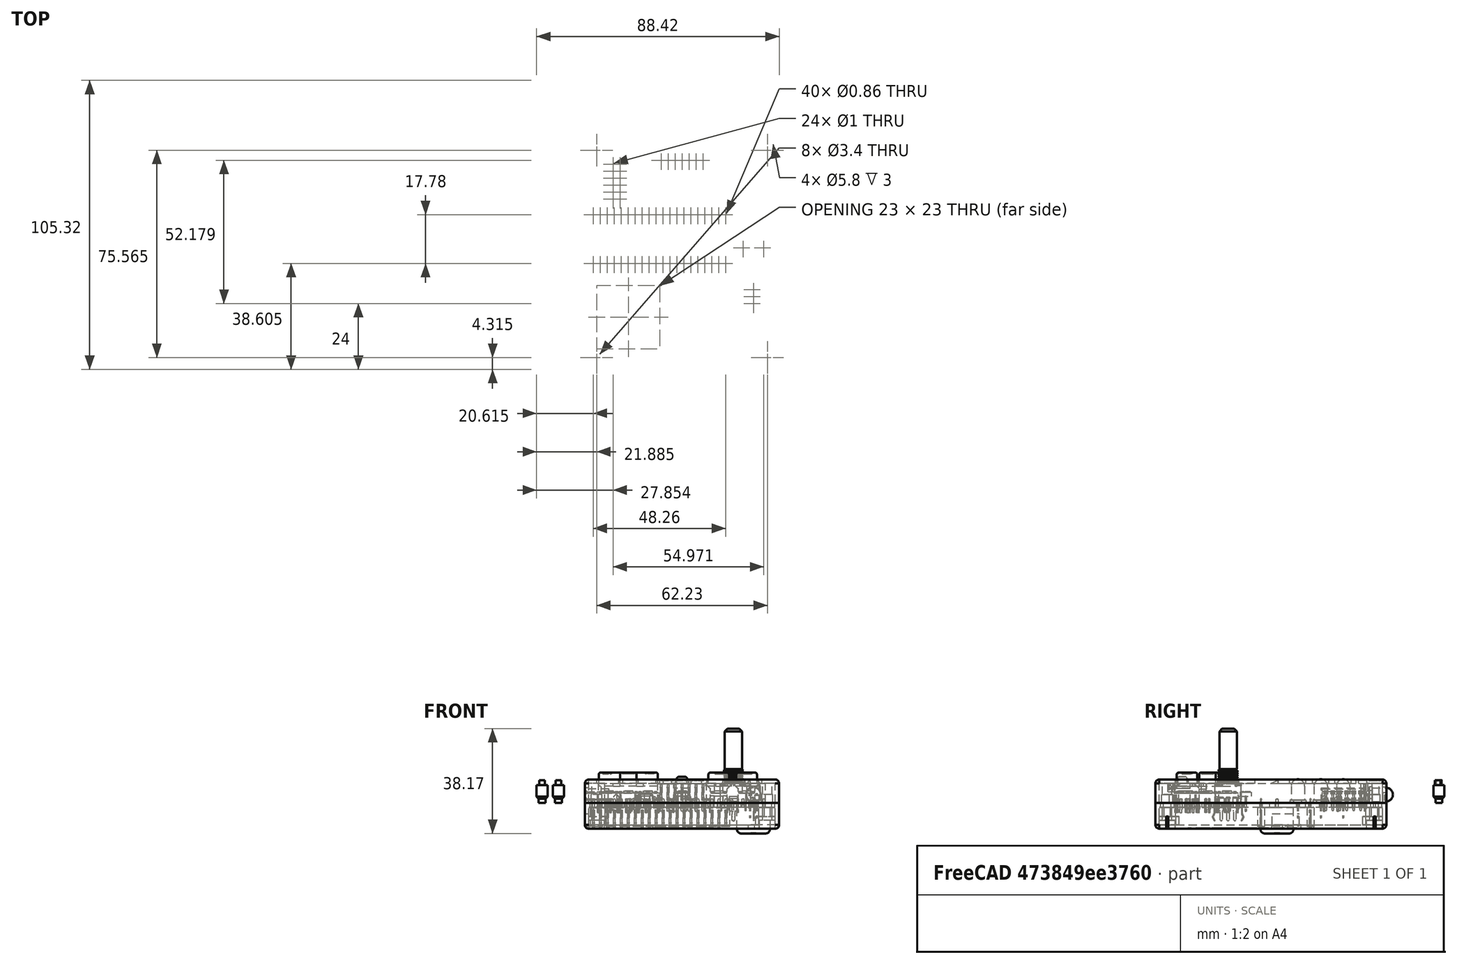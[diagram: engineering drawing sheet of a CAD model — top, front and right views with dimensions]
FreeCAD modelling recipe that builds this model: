
FCSTD DOCUMENT  (FreeCAD 0.19R24276 (Git))
Label: case
License: Creative Commons Attribution-ShareAlike
LicenseURL: http://creativecommons.org/licenses/by-sa/4.0/
objects: Part::FeaturePython×45, Part::Extrusion×42, Part::MultiFuse×27, Part::Cut×25, Part::Feature×22, Part::Part2DObjectPython×20, Part::Box×13, Part::Cylinder×11, Part::Fillet×6, Part::Chamfer×3, Part::Thickness×2
note: 216 computed .brp shape members not serialized (recipe doc carries the construction recipe); baked Part::Feature solids carry a one-line shape summary decoded from their .brp

FEATURE [Part::Cylinder] Cylinder
  Angle = 360
  AttacherType = Attacher::AttachEngine3D
  Height = 5
  Radius = 2
FEATURE [Part::Cylinder] Cylinder001
  Angle = 360
  AttacherType = Attacher::AttachEngine3D
  Height = 1.5
  Placement = pos=(0,0,5) rot=(0,0,1;0rad)
  Radius = 1.25
FEATURE [Part::Cylinder] Cylinder002
  Angle = 360
  AttacherType = Attacher::AttachEngine3D
  Height = 1.8
  Placement = pos=(0,0,-1.8) rot=(0,0,1;0rad)
  Radius = 1
FEATURE [Part::Chamfer] Chamfer
  Base = -> Cylinder
  Edges = 1 edges r=0.75: [Edge1]
FEATURE [Part::FeaturePython] Clone  label="Cylinder003"  # Draft clone (typed FeaturePython)
  AttacherType = Attacher::AttachEngine3D
  Fuse = false
  Objects = -> [Cylinder001]
  Placement = pos=(0,-6,5) rot=(0,0,1;0rad)
  Scale = (1,1,1)
FEATURE [Part::FeaturePython] Clone001  label="Cylinder004"  # Draft clone (typed FeaturePython)
  AttacherType = Attacher::AttachEngine3D
  Fuse = false
  Objects = -> [Cylinder002]
  Placement = pos=(0,-6.4,-1.8) rot=(0,0,1;0rad)
  Scale = (1,1,1)
FEATURE [Part::FeaturePython] Clone002  label="Chamfer001"  # Draft clone (typed FeaturePython)
  AttacherType = Attacher::AttachEngine3D
  Fuse = false
  Objects = -> [Chamfer]
  Placement = pos=(0,-6,0) rot=(0,0,1;0rad)
  Scale = (1,1,1)
FEATURE [Part::MultiFuse] Fusion  label="spacer_desviado"
  Placement = pos=(-45,65,6.5) rot=(0,1,0;3.14159rad)
  Refine = true
  Shapes = -> [Clone,Clone002,Clone001]
FEATURE [Part::MultiFuse] Fusion001  label="spacer_recto"
  Placement = pos=(-51,59,6.5) rot=(0,1,0;3.14159rad)
  Refine = true
  Shapes = -> [Cylinder001,Cylinder002,Chamfer]
FEATURE [Part::Feature] Wire
  shape: bbox 21.5 x 21.5 x 2e-07 mm, 0 faces, 0 solids (baked)
FEATURE [Part::Extrusion] Extrude
  Base = -> Wire
  Dir = (0,0,1)
  DirMode = 2
  FaceMakerClass = Part::FaceMakerBullseye
  LengthFwd = 5
  LengthRev = 0
  Solid = true
  Symmetric = false
FEATURE [Part::Box] Box  label="Cube"
  AttacherType = Attacher::AttachEngine3D
  Height = 1
  Length = 2.5
  Placement = pos=(3,-5.5,0) rot=(0,0,1;0rad)
  Width = 2.5
FEATURE [Part::FeaturePython] Clone003  label="Cube001"  # Draft clone (typed FeaturePython)
  AttacherType = Attacher::AttachEngine3D
  Fuse = false
  Objects = -> [Box]
  Placement = pos=(3,3,0) rot=(0,0,1;0rad)
  Scale = (1,1,1)
FEATURE [Part::FeaturePython] Clone004  label="Cube002"  # Draft clone (typed FeaturePython)
  AttacherType = Attacher::AttachEngine3D
  Fuse = false
  Objects = -> [Clone003]
  Placement = pos=(-5.5,3,0) rot=(0,0,1;0rad)
  Scale = (1,1,1)
FEATURE [Part::FeaturePython] Clone005  label="Cube003"  # Draft clone (typed FeaturePython)
  AttacherType = Attacher::AttachEngine3D
  Fuse = false
  Objects = -> [Clone004]
  Placement = pos=(-5.5,-5.5,0) rot=(0,0,1;0rad)
  Scale = (1,1,1)
FEATURE [Part::Feature] Wire001
  shape: bbox 4.4 x 2.2 x 2e-07 mm, 0 faces, 0 solids (baked)
FEATURE [Part::Feature] Wire002
  shape: bbox 4.4 x 0.5 x 2e-07 mm, 0 faces, 0 solids (baked)
FEATURE [Part::Extrusion] Extrude001
  Base = -> Wire001
  Dir = (0,0,-1)
  DirMode = 2
  FaceMakerClass = Part::FaceMakerBullseye
  LengthFwd = 0.5
  LengthRev = 0
  Placement = pos=(-1e-16,0,0.2) rot=(0,0,1;0rad)
  Solid = true
  Symmetric = false
FEATURE [Part::Extrusion] Extrude002
  Base = -> Wire002
  Dir = (0,0,1)
  DirMode = 2
  FaceMakerClass = Part::FaceMakerBullseye
  LengthFwd = -0.5
  LengthRev = 0
  Placement = pos=(-1e-16,0,0.2) rot=(0,0,1;0rad)
  Solid = true
  Symmetric = false
FEATURE [Part::FeaturePython] Clone006  label="Extrude003"  # Draft clone (typed FeaturePython)
  AttacherType = Attacher::AttachEngine3D
  Fuse = false
  Objects = -> [Extrude001]
  Placement = pos=(-1e-16,-4e-15,0.2) rot=(0,0,1;1.5708rad)
  Scale = (1,1,1)
FEATURE [Part::FeaturePython] Clone007  label="Extrude004"  # Draft clone (typed FeaturePython)
  AttacherType = Attacher::AttachEngine3D
  Fuse = false
  Objects = -> [Extrude002]
  Placement = pos=(-1e-16,-4e-15,0.2) rot=(0,0,1;1.5708rad)
  Scale = (1,1,1)
FEATURE [Part::FeaturePython] Clone008  label="Extrude005"  # Draft clone (typed FeaturePython)
  AttacherType = Attacher::AttachEngine3D
  Fuse = false
  Objects = -> [Extrude001]
  Placement = pos=(1e-15,0,0.2) rot=(0,0,1;3.14159rad)
  Scale = (1,1,1)
FEATURE [Part::FeaturePython] Clone009  label="Extrude006"  # Draft clone (typed FeaturePython)
  AttacherType = Attacher::AttachEngine3D
  Fuse = false
  Objects = -> [Extrude002]
  Placement = pos=(1e-15,0,0.2) rot=(0,0,1;3.14159rad)
  Scale = (1,1,1)
FEATURE [Part::FeaturePython] Clone010  label="Extrude007"  # Draft clone (typed FeaturePython)
  AttacherType = Attacher::AttachEngine3D
  Fuse = false
  Objects = -> [Extrude001]
  Placement = pos=(-1e-16,2e-15,0.2) rot=(0,0,-1;1.5708rad)
  Scale = (1,1,1)
FEATURE [Part::FeaturePython] Clone011  label="Extrude008"  # Draft clone (typed FeaturePython)
  AttacherType = Attacher::AttachEngine3D
  Fuse = false
  Objects = -> [Extrude002]
  Placement = pos=(-1e-16,2e-15,0.2) rot=(0,0,-1;1.5708rad)
  Scale = (1,1,1)
FEATURE [Part::Cylinder] Cylinder003  label="Cylinder005"
  Angle = 360
  AttacherType = Attacher::AttachEngine3D
  Height = 0.5
  Placement = pos=(-1.1e-15,0,4.5) rot=(0,0,1;0rad)
  Radius = 2
FEATURE [Part::FeaturePython] Clone012  label="pcb"  # WARN: FeaturePython — macro-defined, semantics opaque (R4)
  AttacherType = Attacher::AttachEngine3D
  Fuse = false
  Scale = (1,1,1)
FEATURE [Part::Box] Box001  label="Cube004"
  AttacherType = Attacher::AttachEngine3D
  Height = 7.1
  Length = 68
  Placement = pos=(-34,-40.7,0) rot=(0,0,1;0rad)
  Width = 81.4
FEATURE [Part::Thickness] Thickness
  Faces = -> Box001 [Face5]
  Intersection = false
  Join = 0
  Mode = 0
  Placement = pos=(-2e-15,-2.2225,0) rot=(0,0,1;0rad)
  SelfIntersection = false
  Value = 1.4
FEATURE [Part::Part2DObjectPython] Wire003  # Draft 2D object (typed FeaturePython)
  Area = 252.59
  ChamferSize = 0
  Closed = true
  End = (-16.2236,-21.9821,8.4)
  FilletRadius = 0
  Length = 88.8
  MakeFace = true
  Placement = pos=(-16.2236,-14.2321,8.4) rot=(0,0,1;0rad)
  Points = (12) [(0,0,0),(-6.7,0,0),(-6.7,-7.75,0),(-14.45,-7.75,0),(-14.45,-14.45,0),(-6.7,-14.45,0),(-6.7,-22.2,0),(0,-22.2,0),(0,-14.45,0),(7.75,-14.45,0),(7.75,-7.75,0),(0,-7.75,0)]
  Start = (-16.2236,-14.2321,8.4)
  Subdivisions = 0
FEATURE [Part::Extrusion] Extrude003  label="Extrude009"
  Base = -> Wire003
  Dir = (0,0,1)
  DirMode = 2
  FaceMakerClass = Part::FaceMakerBullseye
  LengthFwd = -2
  LengthRev = 0
  Placement = pos=(0,0,0.2) rot=(0,0,1;0rad)
  Solid = false
  Symmetric = false
FEATURE [Part::Cut] Cut009
  Base = -> Thickness
  Refine = true
  Tool = -> Extrude003
FEATURE [Part::Part2DObjectPython] Circle  # Draft 2D object (typed FeaturePython)
  Area = 24.6301
  FirstAngle = 0
  LastAngle = 0
  MakeFace = true
  Placement = pos=(26.035,39.8775,3) rot=(0,0.707107,0.707107;3.14159rad)
  Radius = 2.8
FEATURE [Part::Extrusion] Extrude004  label="Extrude010"
  Base = -> Circle
  Dir = (0,1,-2e-16)
  DirMode = 2
  FaceMakerClass = Part::FaceMakerBullseye
  LengthFwd = -2
  LengthRev = 0
  Solid = false
  Symmetric = false
FEATURE [Part::Cut] Cut010
  Base = -> Cut009
  Refine = true
  Tool = -> Extrude004
FEATURE [Part::Part2DObjectPython] Wire004  # Draft 2D object (typed FeaturePython)
  Area = 22.4
  ChamferSize = 0
  Closed = true
  End = (23.235,39.8775,-1)
  FilletRadius = 0
  Length = 19.2
  MakeFace = true
  Placement = pos=(23.235,39.8775,3) rot=(0,0.707107,0.707107;3.14159rad)
  Points = (4) [(0,0,0),(-5.6,0,0),(-5.6,-4,0),(0,-4,0)]
  Start = (23.235,39.8775,3)
  Subdivisions = 0
FEATURE [Part::Extrusion] Extrude005  label="Extrude011"
  Base = -> Wire004
  Dir = (0,1,-2e-16)
  DirMode = 2
  FaceMakerClass = Part::FaceMakerBullseye
  LengthFwd = -2
  LengthRev = 0
  Solid = false
  Symmetric = false
FEATURE [Part::Cut] Cut011
  Base = -> Cut010
  Refine = true
  Tool = -> Extrude005
FEATURE [Part::Part2DObjectPython] Wire005  # Draft 2D object (typed FeaturePython)
  Area = 18.5
  ChamferSize = 0
  Closed = true
  End = (-22.185,39.8775,3.7)
  FilletRadius = 0
  Length = 17.4
  MakeFace = true
  Placement = pos=(-17.185,39.8775,3.7) rot=(-1,0,0;1.5708rad)
  Points = (4) [(0,0,0),(0,3.7,0),(-5,3.7,0),(-5,-8.88178e-16,0)]
  Start = (-17.185,39.8775,3.7)
  Subdivisions = 0
FEATURE [Part::Extrusion] Extrude006  label="Extrude012"
  Base = -> Wire005
  Dir = (0,1,2e-16)
  DirMode = 2
  FaceMakerClass = Part::FaceMakerBullseye
  LengthFwd = -2
  LengthRev = 0
  Solid = false
  Symmetric = false
FEATURE [Part::Cut] Cut012
  Base = -> Cut011
  Refine = true
  Tool = -> Extrude006
FEATURE [Part::Part2DObjectPython] Wire006  # Draft 2D object (typed FeaturePython)
  Area = 94.3152
  ChamferSize = 0
  Closed = true
  End = (-35.176,16.11,-0.4)
  FilletRadius = 0
  Length = 43.84
  MakeFace = true
  Placement = pos=(-35.176,16.11,5.48) rot=(0.57735,-0.57735,-0.57735;2.0944rad)
  Points = (4) [(0,0,0),(-16.04,0,0),(-16.04,-5.88,0),(0,-5.88,0)]
  Start = (-35.176,16.11,5.48)
  Subdivisions = 0
FEATURE [Part::Extrusion] Extrude007  label="Extrude013"
  Base = -> Wire006
  Dir = (-1,0,0)
  DirMode = 2
  FaceMakerClass = Part::FaceMakerBullseye
  LengthFwd = 2
  LengthRev = 0
  Placement = pos=(1.776,0,0) rot=(0,0,1;0rad)
  Solid = false
  Symmetric = false
FEATURE [Part::Cut] Cut013
  Base = -> Cut012
  Refine = true
  Tool = -> Extrude007
FEATURE [Part::MultiFuse] Fusion002
  Refine = true
  Shapes = -> [Extrude001,Extrude002,Clone006,Clone007,Clone008,Clone009,Clone010,Clone011,Cylinder003]
FEATURE [Part::Cut] Cut
  Base = -> Extrude
  Refine = true
  Tool = -> Fusion002
FEATURE [Part::MultiFuse] Fusion003
  Refine = true
  Shapes = -> [Box,Clone003,Clone004,Clone005,Cut]
FEATURE [Part::Fillet] Fillet
  Base = -> Fusion003
  Edges = 1 edges r=0.45: [Edge110]
FEATURE [Part::Fillet] Fillet001  label="cruceta"
  Base = -> Fillet
  Edges = 12 edges r=0.75: [Edge6,Edge7,Edge8,Edge9,Edge10,Edge11,Edge12,Edge13,Edge14,Edge15,Edge16,Edge17]
  Placement = pos=(-19.5736,-25.3321,6.1) rot=(0,0,1;0rad)
FEATURE [Part::Part2DObjectPython] Circle001  # Draft 2D object (typed FeaturePython)
  Area = 45.3646
  FirstAngle = 0
  LastAngle = 0
  MakeFace = true
  Placement = pos=(18.7277,-17.8234,8.5) rot=(0,0,1;0rad)
  Radius = 3.8
FEATURE [Part::Extrusion] Extrude008  label="Extrude014"
  Base = -> Circle001
  Dir = (0,0,1)
  DirMode = 2
  FaceMakerClass = Part::FaceMakerBullseye
  LengthFwd = -2
  LengthRev = 0
  Solid = false
  Symmetric = false
FEATURE [Part::Cut] Cut014
  Base = -> Cut013
  Refine = true
  Tool = -> Extrude008
FEATURE [Part::FeaturePython] Tube  # WARN: FeaturePython — macro-defined, semantics opaque (R4)
  AttacherType = Attacher::AttachEngine3D
  Height = 7.1
  InnerRadius = 2
  OuterRadius = 3
  Placement = pos=(31.115,35.56,0) rot=(0,0,1;0rad)
FEATURE [Part::FeaturePython] Clone013  label="Tube001"  # Draft clone (typed FeaturePython)
  AttacherType = Attacher::AttachEngine3D
  Fuse = false
  Objects = -> [Tube]
  Placement = pos=(-31.115,35.56,0) rot=(0,0,1;0rad)
  Scale = (1,1,1)
FEATURE [Part::FeaturePython] Clone014  label="Tube002"  # Draft clone (typed FeaturePython)
  AttacherType = Attacher::AttachEngine3D
  Fuse = false
  Objects = -> [Clone013]
  Placement = pos=(-31.115,-40.005,0) rot=(0,0,1;0rad)
  Scale = (1,1,1)
FEATURE [Part::FeaturePython] Clone015  label="Tube003"  # Draft clone (typed FeaturePython)
  AttacherType = Attacher::AttachEngine3D
  Fuse = false
  Objects = -> [Clone014]
  Placement = pos=(31.115,-40.005,0) rot=(0,0,1;0rad)
  Scale = (1,1,1)
FEATURE [Part::MultiFuse] Fusion004  label="unio"
  Refine = true
  Shapes = -> [Cut014,Tube,Clone013,Clone014,Clone015]
FEATURE [Part::Box] Box002  label="Cube005"
  AttacherType = Attacher::AttachEngine3D
  Height = 2
  Length = 44
  Placement = pos=(-22,-4.641,7.1) rot=(0,0,1;0rad)
  Width = 39
FEATURE [Part::Cut] Cut015
  Base = -> Fusion004
  Refine = true
  Tool = -> Box002
FEATURE [Part::Part2DObjectPython] Circle002  # Draft 2D object (typed FeaturePython)
  Area = 28.2743
  FirstAngle = 0
  LastAngle = 0
  MakeFace = true
  Placement = pos=(26.035,24.13,8.5) rot=(0,0,1;0rad)
  Radius = 3
FEATURE [Part::Extrusion] Extrude009  label="Extrude015"
  Base = -> Circle002
  Dir = (0,0,1)
  DirMode = 2
  FaceMakerClass = Part::FaceMakerBullseye
  LengthFwd = -2
  LengthRev = 0
  Solid = false
  Symmetric = false
FEATURE [Part::FeaturePython] Clone016  label="Extrude016"  # Draft clone (typed FeaturePython)
  AttacherType = Attacher::AttachEngine3D
  Fuse = false
  Objects = -> [Extrude009]
  Placement = pos=(-7.1e-15,-8.175,0) rot=(0,0,1;0rad)
  Scale = (1,1,1)
FEATURE [Part::FeaturePython] Clone017  label="Extrude017"  # Draft clone (typed FeaturePython)
  AttacherType = Attacher::AttachEngine3D
  Fuse = false
  Objects = -> [Clone016]
  Placement = pos=(-4e-15,-16.51,0) rot=(0,0,1;0rad)
  Scale = (1,1,1)
FEATURE [Part::MultiFuse] Fusion005
  Refine = true
  Shapes = -> [Extrude009,Clone016,Clone017]
FEATURE [Part::Cut] Cut016
  Base = -> Cut015
  Refine = true
  Tool = -> Fusion005
FEATURE [Part::Part2DObjectPython] Circle003  # Draft 2D object (typed FeaturePython)
  Area = 50.2655
  FirstAngle = 0
  LastAngle = 0
  MakeFace = true
  Placement = pos=(23.545,-32.77,8.5) rot=(0,0,1;0rad)
  Radius = 4
FEATURE [Part::Extrusion] Extrude010  label="Extrude018"
  Base = -> Circle003
  Dir = (0,0,1)
  DirMode = 2
  FaceMakerClass = Part::FaceMakerBullseye
  LengthFwd = -2
  LengthRev = 0
  Solid = false
  Symmetric = false
FEATURE [Part::FeaturePython] Clone018  label="Extrude019"  # Draft clone (typed FeaturePython)
  AttacherType = Attacher::AttachEngine3D
  Fuse = false
  Objects = -> [Extrude010]
  Placement = pos=(-10.16,0,0) rot=(0,0,1;0rad)
  Scale = (1,1,1)
FEATURE [Part::Part2DObjectPython] Circle004  # Draft 2D object (typed FeaturePython)
  Area = 18.0956
  FirstAngle = 0
  LastAngle = 0
  MakeFace = true
  Placement = pos=(-0.025,-34.635,8.5) rot=(0,0,1;0rad)
  Radius = 2.4
FEATURE [Part::Extrusion] Extrude011  label="Extrude020"
  Base = -> Circle004
  Dir = (0,0,1)
  DirMode = 2
  FaceMakerClass = Part::FaceMakerBullseye
  LengthFwd = -2
  LengthRev = 0
  Solid = false
  Symmetric = false
FEATURE [Part::MultiFuse] Fusion006
  Refine = true
  Shapes = -> [Extrude010,Clone018,Extrude011]
FEATURE [Part::Cut] Cut017
  Base = -> Cut016
  Refine = true
  Tool = -> Fusion006
FEATURE [Part::Part2DObjectPython] Circle005  # Draft 2D object (typed FeaturePython)
  Area = 38.4845
  FirstAngle = 0
  LastAngle = 0
  MakeFace = true
  Placement = pos=(-0.23,-11.43,8.5) rot=(0,0,1;0rad)
  Radius = 3.5
FEATURE [Part::Extrusion] Extrude012  label="Extrude021"
  Base = -> Circle005
  Dir = (0,0,1)
  DirMode = 2
  FaceMakerClass = Part::FaceMakerBullseye
  LengthFwd = -2
  LengthRev = 0
  Solid = false
  Symmetric = false
FEATURE [Part::Cut] Cut018  label="union"
  Base = -> Cut017
  Refine = true
  Tool = -> Extrude012
FEATURE [Part::Part2DObjectPython] Wire007  # Draft 2D object (typed FeaturePython)
  Area = 266
  ChamferSize = 0
  Closed = true
  End = (-16.0736,-14.0821,8.5)
  FilletRadius = 0
  Length = 90
  MakeFace = true
  Placement = pos=(-23.0736,-14.0821,8.5) rot=(0,0,1;0rad)
  Points = (12) [(0,0,0),(0,-7.75,0),(-7.75,-7.75,0),(-7.75,-14.75,0),(0,-14.75,0),(0,-22.5,0),(7,-22.5,0),(7,-14.75,0),(14.75,-14.75,0),(14.75,-7.75,0),(7,-7.75,0),(7,0,0)]
  Start = (-23.0736,-14.0821,8.5)
  Subdivisions = 0
FEATURE [Part::Extrusion] Extrude013  label="Extrude022"
  Base = -> Wire007
  Dir = (0,0,1)
  DirMode = 2
  FaceMakerClass = Part::FaceMakerBullseye
  LengthFwd = -2
  LengthRev = 0
  Solid = false
  Symmetric = false
FEATURE [Part::Cut] Cut019  label="superior"
  Base = -> Cut018
  Refine = true
  Tool = -> Extrude013
FEATURE [Part::Box] Box003  label="marco_superior_pantalla"
  AttacherType = Attacher::AttachEngine3D
  Height = 1.4
  Length = 44
  Placement = pos=(-22,28.859,7.1) rot=(0,0,1;0rad)
  Width = 5.5
FEATURE [Part::Box] Box004  label="hueco_pins_oled"
  AttacherType = Attacher::AttachEngine3D
  Height = 1.1
  Length = 19
  Placement = pos=(-9.5,29.759,7.1) rot=(0,0,1;0rad)
  Width = 3
FEATURE [Part::Cut] Cut020  label="marco_superior_pantalla001"
  Base = -> Box003
  Refine = true
  Tool = -> Box004
FEATURE [Part::Box] Box005  label="Cube006"
  AttacherType = Attacher::AttachEngine3D
  Height = 1.4
  Length = 44
  Placement = pos=(-22,-4.641,7.1) rot=(0,0,1;0rad)
  Width = 5
FEATURE [Part::Box] Box006  label="Cube007"
  AttacherType = Attacher::AttachEngine3D
  Height = 1.4
  Length = 14
  Placement = pos=(-7,-8.16668,2.88956) rot=(1,0,0;0.42638rad)
  Width = 10
FEATURE [Part::Cut] Cut021  label="marco_inferior_pantalla"
  Base = -> Box005
  Refine = true
  Tool = -> Box006
FEATURE [Part::MultiFuse] Fusion007  label="superior001"
  Refine = true
  Shapes = -> [Cut019,Cut020,Cut021]
FEATURE [Part::FeaturePython] Tube001  label="Tube004"  # WARN: FeaturePython — macro-defined, semantics opaque (R4)
  AttacherType = Attacher::AttachEngine3D
  Height = 4.1
  InnerRadius = 1.7
  OuterRadius = 2.1
  Placement = pos=(31.115,35.56,3) rot=(0,0,1;0rad)
FEATURE [Part::FeaturePython] Clone019  label="Tube005"  # Draft clone (typed FeaturePython)
  AttacherType = Attacher::AttachEngine3D
  Fuse = false
  Objects = -> [Tube001]
  Placement = pos=(-31.115,35.56,3) rot=(0,0,1;0rad)
  Scale = (1,1,1)
FEATURE [Part::FeaturePython] Clone020  label="Tube006"  # Draft clone (typed FeaturePython)
  AttacherType = Attacher::AttachEngine3D
  Fuse = false
  Objects = -> [Clone019]
  Placement = pos=(-31.115,-40.005,3) rot=(0,0,1;0rad)
  Scale = (1,1,1)
FEATURE [Part::FeaturePython] Clone021  label="Tube007"  # Draft clone (typed FeaturePython)
  AttacherType = Attacher::AttachEngine3D
  Fuse = false
  Objects = -> [Clone020]
  Placement = pos=(31.115,-40.005,3) rot=(0,0,1;0rad)
  Scale = (1,1,1)
FEATURE [Part::MultiFuse] Fusion008  label="superior002"
  Refine = true
  Shapes = -> [Fusion007,Tube001,Clone019,Clone020,Clone021]
FEATURE [Part::Cylinder] Cylinder004  label="Cylinder006"
  Angle = 360
  AttacherType = Attacher::AttachEngine3D
  Height = 5
  Placement = pos=(69.0093,-36.5313,0) rot=(0,0,1;0rad)
  Radius = 3.75
FEATURE [Part::Cylinder] Cylinder005  label="Cylinder007"
  Angle = 360
  AttacherType = Attacher::AttachEngine3D
  Height = 1
  Placement = pos=(69.0093,-36.5313,0) rot=(0,0,1;0rad)
  Radius = 4.75
FEATURE [Part::Feature] path833
  Placement = pos=(68.9799,-36.5544,5) rot=(0,0,1;0rad)
  shape: bbox 3.774 x 3.6 x 2e-07 mm, 0 faces, 0 solids (baked)
FEATURE [Part::Feature] path833001
  Placement = pos=(68.9799,-36.5544,5) rot=(0,0,1;0rad)
  shape: bbox 0.9863 x 1.432 x 2e-07 mm, 0 faces, 0 solids (baked)
FEATURE [Part::Extrusion] Extrude014  label="Extrude023"
  Base = -> path833
  Dir = (0,0,-1)
  DirMode = 2
  FaceMakerClass = Part::FaceMakerBullseye
  LengthFwd = 0.5
  LengthRev = 0
  Solid = true
  Symmetric = false
FEATURE [Part::Extrusion] Extrude015  label="Extrude024"
  Base = -> path833001
  Dir = (0,0,1)
  DirMode = 2
  FaceMakerClass = Part::FaceMakerBullseye
  LengthFwd = -0.5
  LengthRev = 0
  Solid = true
  Symmetric = false
FEATURE [Part::FeaturePython] Clone022  label="Cylinder008"  # Draft clone (typed FeaturePython)
  AttacherType = Attacher::AttachEngine3D
  Fuse = false
  Objects = -> [Cylinder004]
  Placement = pos=(54.0093,-36.5313,0) rot=(0,0,1;0rad)
  Scale = (1,1,1)
FEATURE [Part::FeaturePython] Clone023  label="Cylinder009"  # Draft clone (typed FeaturePython)
  AttacherType = Attacher::AttachEngine3D
  Fuse = false
  Objects = -> [Cylinder005]
  Placement = pos=(54.0093,-36.5313,0) rot=(0,0,1;0rad)
  Scale = (1,1,1)
FEATURE [Part::Cut] Cut022
  Base = -> Cylinder004
  Refine = true
  Tool = -> Extrude014
FEATURE [Part::MultiFuse] Fusion009  label="union001"
  Placement = pos=(-45.4643,3.76128,6.1) rot=(0,0,1;0rad)
  Refine = true
  Shapes = -> [Cylinder005,Extrude015,Cut022]
FEATURE [Part::Feature] path833002
  Placement = pos=(54.066,-36.5448,5) rot=(0,0,1;0rad)
  shape: bbox 0.9598 x 0.7621 x 2e-07 mm, 0 faces, 0 solids (baked)
FEATURE [Part::Feature] path833003
  Placement = pos=(54.066,-36.5448,5) rot=(0,0,1;0rad)
  shape: bbox 1.107 x 0.9429 x 2e-07 mm, 0 faces, 0 solids (baked)
FEATURE [Part::Feature] path833004
  Placement = pos=(54.066,-36.5448,5) rot=(0,0,1;0rad)
  shape: bbox 2.964 x 3.6 x 2e-07 mm, 0 faces, 0 solids (baked)
FEATURE [Part::Extrusion] Extrude016  label="Extrude025"
  Base = -> path833002
  Dir = (0,0,1)
  DirMode = 2
  FaceMakerClass = Part::FaceMakerBullseye
  LengthFwd = -0.5
  LengthRev = 0
  Solid = true
  Symmetric = false
FEATURE [Part::Extrusion] Extrude017  label="Extrude026"
  Base = -> path833003
  Dir = (0,0,1)
  DirMode = 2
  FaceMakerClass = Part::FaceMakerBullseye
  LengthFwd = -0.5
  LengthRev = 0
  Solid = true
  Symmetric = false
FEATURE [Part::Extrusion] Extrude018  label="Extrude027"
  Base = -> path833004
  Dir = (0,0,-1)
  DirMode = 2
  FaceMakerClass = Part::FaceMakerBullseye
  LengthFwd = 0.5
  LengthRev = 0
  Solid = true
  Symmetric = false
FEATURE [Part::Cut] Cut023
  Base = -> Clone022
  Refine = true
  Tool = -> Extrude018
FEATURE [Part::MultiFuse] Fusion010  label="union002"
  Placement = pos=(-40.6243,3.76128,6.1) rot=(0,0,1;0rad)
  Refine = true
  Shapes = -> [Clone023,Extrude016,Extrude017,Cut023]
FEATURE [Part::Fillet] Fillet002  label="tecla_a"
  Base = -> Fusion009
  Edges = 1 edges r=0.75: [Edge6]
FEATURE [Part::Fillet] Fillet003  label="tecla_b"
  Base = -> Fusion010
  Edges = 1 edges r=0.75: [Edge6]
FEATURE [Part::Part2DObjectPython] Circle006  # Draft 2D object (typed FeaturePython)
  Area = 58.088
  FirstAngle = 0
  LastAngle = 0
  MakeFace = true
  Placement = pos=(23.545,-32.77,8.5) rot=(0,0,1;0rad)
  Radius = 4.3
FEATURE [Part::Extrusion] Extrude019  label="Extrude028"
  Base = -> Circle006
  Dir = (0,0,1)
  DirMode = 2
  FaceMakerClass = Part::FaceMakerBullseye
  LengthFwd = -4
  LengthRev = 0
  Solid = false
  Symmetric = false
FEATURE [Part::FeaturePython] Clone024  label="Extrude029"  # Draft clone (typed FeaturePython)
  AttacherType = Attacher::AttachEngine3D
  Fuse = false
  Objects = -> [Extrude019]
  Placement = pos=(-10.16,0,0) rot=(0,0,1;0rad)
  Scale = (1,1,1)
FEATURE [Part::Box] Box007  label="Cube008"
  AttacherType = Attacher::AttachEngine3D
  Height = 3
  Length = 1.5
  Placement = pos=(20.545,-39.77,4.1) rot=(0,0,1;0rad)
  Width = 14
FEATURE [Part::FeaturePython] Clone025  label="Cube009"  # Draft clone (typed FeaturePython)
  AttacherType = Attacher::AttachEngine3D
  Fuse = false
  Objects = -> [Box007]
  Placement = pos=(25.045,-39.77,4.1) rot=(0,0,1;0rad)
  Scale = (1,1,1)
FEATURE [Part::FeaturePython] Clone026  label="Cube010"  # Draft clone (typed FeaturePython)
  AttacherType = Attacher::AttachEngine3D
  Fuse = false
  Objects = -> [Clone025]
  Placement = pos=(14.885,-39.77,4.1) rot=(0,0,1;0rad)
  Scale = (1,1,1)
FEATURE [Part::FeaturePython] Clone027  label="Cube011"  # Draft clone (typed FeaturePython)
  AttacherType = Attacher::AttachEngine3D
  Fuse = false
  Objects = -> [Box007]
  Placement = pos=(10.385,-39.77,4.1) rot=(0,0,1;0rad)
  Scale = (1,1,1)
FEATURE [Part::Part2DObjectPython] Circle007  # Draft 2D object (typed FeaturePython)
  Area = 91.6088
  FirstAngle = 0
  LastAngle = 0
  MakeFace = true
  Placement = pos=(23.545,-32.77,7.1) rot=(1,0,0;3.14159rad)
  Radius = 5.4
FEATURE [Part::Extrusion] Extrude020  label="Extrude030"
  Base = -> Circle007
  Dir = (0,0,-1)
  DirMode = 2
  FaceMakerClass = Part::FaceMakerBullseye
  LengthFwd = 3
  LengthRev = 0
  Solid = false
  Symmetric = false
FEATURE [Part::FeaturePython] Clone028  label="Extrude031"  # Draft clone (typed FeaturePython)
  AttacherType = Attacher::AttachEngine3D
  Fuse = false
  Objects = -> [Extrude020]
  Placement = pos=(-10.16,0,0) rot=(0,0,1;0rad)
  Scale = (1,1,1)
FEATURE [Part::Box] Box008  label="Cube012"
  AttacherType = Attacher::AttachEngine3D
  Height = 1
  Length = 2
  Placement = pos=(22.545,-38.77,6.1) rot=(0,0,1;0rad)
  Width = 12
FEATURE [Part::FeaturePython] Clone029  label="Cube013"  # Draft clone (typed FeaturePython)
  AttacherType = Attacher::AttachEngine3D
  Fuse = false
  Objects = -> [Box008]
  Placement = pos=(12.385,-38.77,6.1) rot=(0,0,1;0rad)
  Scale = (1,1,1)
FEATURE [Part::MultiFuse] Fusion012  label="tecla_b001"
  Refine = true
  Shapes = -> [Clone029,Fillet003]
FEATURE [Part::MultiFuse] Fusion013  label="tecla_a001"
  Refine = true
  Shapes = -> [Box008,Fillet002]
FEATURE [Part::MultiFuse] Fusion015
  Refine = true
  Shapes = -> [Extrude019,Clone024,Extrude020,Clone028]
FEATURE [Part::MultiFuse] Fusion016
  Refine = true
  Shapes = -> [Fusion008,Box007,Clone025,Clone026,Clone027]
FEATURE [Part::Cut] Cut024  label="superior003"
  Base = -> Fusion016
  Refine = true
  Tool = -> Fusion015
FEATURE [Part::Cylinder] Cylinder006  label="Cylinder010"
  Angle = 360
  AttacherType = Attacher::AttachEngine3D
  Height = 1.8
  Placement = pos=(0,0,-0.3) rot=(0,0,1;0rad)
  Radius = 3
FEATURE [Part::Cylinder] Cylinder007  label="Cylinder011"
  Angle = 360
  AttacherType = Attacher::AttachEngine3D
  Height = 2.4
  Placement = pos=(0,0,1.5) rot=(0,0,1;0rad)
  Radius = 1.9
FEATURE [Part::MultiFuse] Fusion017
  Shapes = -> [Cylinder006,Cylinder007]
FEATURE [Part::Fillet] Fillet004  label="tecla_reset"
  Base = -> Fusion017
  Edges = 1 edges r=0.75: [Edge5]
  Placement = pos=(-0.025,-34.635,5.6) rot=(0,0,1;0rad)
FEATURE [Part::Box] Box009  label="Cube014"
  AttacherType = Attacher::AttachEngine3D
  Height = 1.4
  Length = 0.5
  Placement = pos=(21.5,0.359,7.1) rot=(0,0,1;0rad)
  Width = 28.5
FEATURE [Part::FeaturePython] Clone030  label="Cube015"  # Draft clone (typed FeaturePython)
  AttacherType = Attacher::AttachEngine3D
  Fuse = false
  Objects = -> [Box009]
  Placement = pos=(-22,0.359,7.1) rot=(0,0,1;0rad)
  Scale = (1,1,1)
FEATURE [Part::MultiFuse] Fusion018  label="superior004"
  Shapes = -> [Cut024,Box009,Clone030]
FEATURE [Part::Box] Box010  label="Cube016"
  AttacherType = Attacher::AttachEngine3D
  Height = 8
  Length = 68
  Placement = pos=(-34,-42.9225,-8) rot=(0,0,1;0rad)
  Width = 81.4
FEATURE [Part::Thickness] Thickness001
  Faces = -> Box010 [Face6]
  Intersection = false
  Join = 0
  Mode = 0
  SelfIntersection = false
  Value = 1.4
FEATURE [Part::Part2DObjectPython] Circle008  # Draft 2D object (typed FeaturePython)
  Area = 0
  FirstAngle = 0
  LastAngle = 0
  MakeFace = false
  Placement = pos=(26.025,0,-9.4) rot=(0.707107,0.707107,0;3.14159rad)
  Radius = 2
FEATURE [Part::Extrusion] Extrude021  label="hueco_buzzer"
  Base = -> Circle008
  Dir = (0,0,-1)
  DirMode = 2
  FaceMakerClass = Part::FaceMakerBullseye
  LengthFwd = -1.4
  LengthRev = 0
  Solid = true
  Symmetric = false
FEATURE [Part::Part2DObjectPython] Circle009  # Draft 2D object (typed FeaturePython)
  Area = 0
  FirstAngle = 0
  LastAngle = 0
  MakeFace = false
  Placement = pos=(-21.845,6.275,-9.4) rot=(0.707107,0.707107,0;3.14159rad)
  Radius = 2.5
FEATURE [Part::Extrusion] Extrude022  label="hueco_boot"
  Base = -> Circle009
  Dir = (0,0,-1)
  DirMode = 2
  FaceMakerClass = Part::FaceMakerBullseye
  LengthFwd = -1.4
  LengthRev = 0
  Solid = true
  Symmetric = false
FEATURE [Part::Box] Box011  label="hueco_microusb"
  AttacherType = Attacher::AttachEngine3D
  Height = 4.5
  Length = 6.5
  Placement = pos=(-35.4,-1.825,-8.4) rot=(0,0,1;0rad)
  Width = 10
FEATURE [Part::Box] Box012  label="hueco_bateria"
  AttacherType = Attacher::AttachEngine3D
  Height = 1.4
  Length = 53
  Placement = pos=(-26.5,13.4775,-9.4) rot=(0,0,1;0rad)
  Width = 25
FEATURE [Part::MultiFuse] Fusion019
  Shapes = -> [Extrude021,Extrude022,Box011,Box012]
FEATURE [Part::Cut] Cut025
  Base = -> Thickness001
  Tool = -> Fusion019
FEATURE [Part::Cylinder] Cylinder008  label="neg"
  Angle = 360
  AttacherType = Attacher::AttachEngine3D
  Height = 3
  Placement = pos=(31.115,35.56,-9.4) rot=(0,0,1;0rad)
  Radius = 2.9
FEATURE [Part::Cylinder] Cylinder009  label="pos"
  Angle = 360
  AttacherType = Attacher::AttachEngine3D
  Height = 4.4
  Placement = pos=(31.115,35.56,-9.4) rot=(0,0,1;0rad)
  Radius = 4.3
FEATURE [Part::FeaturePython] Tube002  label="pos001"  # WARN: FeaturePython — macro-defined, semantics opaque (R4)
  AttacherType = Attacher::AttachEngine3D
  Height = 3.4
  InnerRadius = 1.7
  OuterRadius = 3.1
  Placement = pos=(31.115,35.56,-5) rot=(0,0,1;0rad)
FEATURE [Part::MultiFuse] Fusion020
  Shapes = -> [Cylinder009,Tube002]
FEATURE [Part::Fillet] Fillet005
  Base = -> Fusion020
  Edges = 1 edges r=1.4: [Edge3]
FEATURE [Part::FeaturePython] Clone031  label="neg001"  # Draft clone (typed FeaturePython)
  AttacherType = Attacher::AttachEngine3D
  Fuse = false
  Objects = -> [Cylinder008]
  Placement = pos=(-31.115,35.56,-9.4) rot=(0,0,1;0rad)
  Scale = (1,1,1)
FEATURE [Part::FeaturePython] Clone032  label="Fillet006"  # Draft clone (typed FeaturePython)
  AttacherType = Attacher::AttachEngine3D
  Fuse = false
  Objects = -> [Fillet005]
  Placement = pos=(-62.23,0,0) rot=(0,0,1;0rad)
  Scale = (1,1,1)
FEATURE [Part::FeaturePython] Clone033  label="Fillet007"  # Draft clone (typed FeaturePython)
  AttacherType = Attacher::AttachEngine3D
  Fuse = false
  Objects = -> [Clone032]
  Placement = pos=(-62.23,-75.565,0) rot=(0,0,1;0rad)
  Scale = (1,1,1)
FEATURE [Part::FeaturePython] Clone034  label="neg002"  # Draft clone (typed FeaturePython)
  AttacherType = Attacher::AttachEngine3D
  Fuse = false
  Objects = -> [Clone031]
  Placement = pos=(-31.115,-40.005,-9.4) rot=(0,0,1;0rad)
  Scale = (1,1,1)
FEATURE [Part::FeaturePython] Clone035  label="neg003"  # Draft clone (typed FeaturePython)
  AttacherType = Attacher::AttachEngine3D
  Fuse = false
  Objects = -> [Clone034]
  Placement = pos=(31.115,-40.005,-9.4) rot=(0,0,1;0rad)
  Scale = (1,1,1)
FEATURE [Part::FeaturePython] Clone036  label="Fillet008"  # Draft clone (typed FeaturePython)
  AttacherType = Attacher::AttachEngine3D
  Fuse = false
  Objects = -> [Clone033]
  Placement = pos=(7.1e-15,-75.565,0) rot=(0,0,1;0rad)
  Scale = (1,1,1)
FEATURE [Part::MultiFuse] Fusion021
  Shapes = -> [Cut025,Fillet005,Clone032,Clone033,Clone036]
FEATURE [Part::MultiFuse] Fusion022
  Shapes = -> [Cylinder008,Clone031,Clone034,Clone035]
FEATURE [Part::Cut] Cut026
  Base = -> Fusion021
  Tool = -> Fusion022
FEATURE [Part::Cylinder] Cylinder010  label="Cylinder012"
  Angle = 360
  AttacherType = Attacher::AttachEngine3D
  Height = 10
  Placement = pos=(31.115,35.56,-11.6) rot=(0,0,1;0rad)
  Radius = 1.7
FEATURE [Part::FeaturePython] Clone037  label="Cylinder013"  # Draft clone (typed FeaturePython)
  AttacherType = Attacher::AttachEngine3D
  Fuse = false
  Objects = -> [Cylinder010]
  Placement = pos=(31.115,-40.005,-11.6) rot=(0,0,1;0rad)
  Scale = (1,1,1)
FEATURE [Part::FeaturePython] Clone038  label="Cylinder014"  # Draft clone (typed FeaturePython)
  AttacherType = Attacher::AttachEngine3D
  Fuse = false
  Objects = -> [Clone037]
  Placement = pos=(-31.115,-40.005,-11.6) rot=(0,0,1;0rad)
  Scale = (1,1,1)
FEATURE [Part::FeaturePython] Clone039  label="Cylinder015"  # Draft clone (typed FeaturePython)
  AttacherType = Attacher::AttachEngine3D
  Fuse = false
  Objects = -> [Clone038]
  Placement = pos=(-31.115,35.56,-11.6) rot=(0,0,1;0rad)
  Scale = (1,1,1)
FEATURE [Part::MultiFuse] Fusion023
  Shapes = -> [Clone039,Cylinder010,Clone037,Clone038]
FEATURE [Part::Cut] Cut027  label="inferior"
  Base = -> Cut026
  Tool = -> Fusion023
FEATURE [Part::Part2DObjectPython] Circle010  # Draft 2D object (typed FeaturePython)
  Area = 0
  FirstAngle = 0
  LastAngle = 0
  MakeFace = false
  Placement = pos=(-35.4,33.0694,3.80513) rot=(0.57735,-0.57735,-0.57735;2.0944rad)
  Radius = 0.5
FEATURE [Part::Extrusion] Extrude023  label="Extrude032"
  Base = -> Circle010
  Dir = (-1,0,0)
  DirMode = 2
  FaceMakerClass = Part::FaceMakerBullseye
  LengthFwd = -0.6
  LengthRev = 0
  Solid = true
  Symmetric = false
FEATURE [Part::Cut] Cut028  label="superior005"
  Base = -> Fusion018
  Tool = -> Extrude023
FEATURE [Part::Part2DObjectPython] Circle011  # Draft 2D object (typed FeaturePython)
  Area = 0
  FirstAngle = 0
  LastAngle = 0
  MakeFace = false
  Placement = pos=(-23.9659,39.8775,1.88448) rot=(-1,0,0;1.5708rad)
  Radius = 1
FEATURE [Part::Part2DObjectPython] Rectangle  # Draft 2D object (typed FeaturePython)
  Area = 0
  ChamferSize = 0
  Columns = 1
  FilletRadius = 0
  Height = 0.6
  Length = 2
  MakeFace = false
  Placement = pos=(-16.0659,39.8775,0.884482) rot=(0.57735,0.57735,0.57735;4.18879rad)
  Rows = 1
FEATURE [Part::Extrusion] Extrude024  label="Extrude033"
  Base = -> Circle011
  Dir = (0,1,2e-16)
  DirMode = 2
  FaceMakerClass = Part::FaceMakerBullseye
  LengthFwd = -0.6
  LengthRev = 0
  Solid = true
  Symmetric = false
FEATURE [Part::Extrusion] Extrude025  label="Extrude034"
  Base = -> Rectangle
  Dir = (-2e-16,1,0)
  DirMode = 2
  FaceMakerClass = Part::FaceMakerBullseye
  LengthFwd = -0.6
  LengthRev = 0
  Solid = true
  Symmetric = false
FEATURE [Part::MultiFuse] Fusion024
  Shapes = -> [Extrude024,Extrude025]
FEATURE [Part::Cut] Cut029  label="superior006"
  Base = -> Cut028
  Tool = -> Fusion024
FEATURE [Part::Feature] Face
  shape: bbox 2.186 x 2.095 x 2e-07 mm, 1 faces, 0 solids (baked)
FEATURE [Part::Extrusion] Extrude026  label="Extrude035"
  Base = -> Face
  Dir = (0,0,-1)
  DirMode = 2
  FaceMakerClass = Part::FaceMakerBullseye
  LengthFwd = -7.1
  LengthRev = 0
  Solid = false
  Symmetric = false
FEATURE [Part::Feature] Face001
  shape: bbox 2.186 x 2.095 x 2e-07 mm, 1 faces, 0 solids (baked)
FEATURE [Part::Extrusion] Extrude027  label="Extrude036"
  Base = -> Face001
  Dir = (0,0,-1)
  DirMode = 2
  FaceMakerClass = Part::FaceMakerBullseye
  LengthFwd = -7.1
  LengthRev = 0
  Solid = false
  Symmetric = false
FEATURE [Part::Feature] Face002
  shape: bbox 2.186 x 2.095 x 2e-07 mm, 1 faces, 0 solids (baked)
FEATURE [Part::Extrusion] Extrude028  label="Extrude037"
  Base = -> Face002
  Dir = (0,0,-1)
  DirMode = 2
  FaceMakerClass = Part::FaceMakerBullseye
  LengthFwd = -7.1
  LengthRev = 0
  Solid = false
  Symmetric = false
FEATURE [Part::Feature] Face003
  shape: bbox 2.186 x 2.095 x 2e-07 mm, 1 faces, 0 solids (baked)
FEATURE [Part::Extrusion] Extrude029  label="Extrude038"
  Base = -> Face003
  Dir = (0,0,-1)
  DirMode = 2
  FaceMakerClass = Part::FaceMakerBullseye
  LengthFwd = -7.1
  LengthRev = 0
  Solid = false
  Symmetric = false
FEATURE [Part::MultiFuse] Fusion025
  Shapes = -> [Cut029,Extrude026,Extrude027,Extrude028,Extrude029]
FEATURE [Part::Chamfer] Chamfer001  label="Chamfer002"
  Base = -> Fusion025
  Edges = 7 edges r=2: [Edge164,Edge166,Edge172,Edge174,Edge180,Edge184,Edge186]
FEATURE [Part::Chamfer] Chamfer002  label="superior007"
  Base = -> Chamfer001
  Edges = 1 edges r=1.55: [Edge70]
FEATURE [Part::Part2DObjectPython] Wire008  # Draft 2D object (typed FeaturePython)
  Area = 0
  ChamferSize = 0
  Closed = true
  End = (-16.0736,-13.8321,7.1)
  FilletRadius = 0
  Length = 14.5
  MakeFace = false
  Placement = pos=(-16.0736,-14.0821,7.1) rot=(1,0,0;3.14159rad)
  Points = (4) [(0,0,0),(-7,0,0),(-7,-0.25,0),(0,-0.25,0)]
  Start = (-16.0736,-14.0821,7.1)
  Subdivisions = 0
FEATURE [Part::Extrusion] Extrude030  label="Extrude039"
  Base = -> Wire008
  Dir = (0,0,-1)
  DirMode = 2
  FaceMakerClass = Part::FaceMakerBullseye
  LengthFwd = -3
  LengthRev = 0
  Solid = true
  Symmetric = false
FEATURE [Part::FeaturePython] Clone040  label="Extrude040"  # Draft clone (typed FeaturePython)
  AttacherType = Attacher::AttachEngine3D
  Fuse = false
  Objects = -> [Extrude030]
  Placement = pos=(0,-22.75,0) rot=(0,0,1;0rad)
  Scale = (1,1,1)
FEATURE [Part::Part2DObjectPython] Wire009  # Draft 2D object (typed FeaturePython)
  Area = 0
  ChamferSize = 0
  Closed = true
  End = (-8.07358,-28.8321,7.1)
  FilletRadius = 0
  Length = 14.5
  MakeFace = false
  Placement = pos=(-8.32358,-28.8321,7.1) rot=(1,0,0;3.14159rad)
  Points = (4) [(0,0,0),(3.55271e-15,-7,0),(0.25,-7,0),(0.25,0,0)]
  Start = (-8.32358,-28.8321,7.1)
  Subdivisions = 0
FEATURE [Part::Extrusion] Extrude031  label="Extrude041"
  Base = -> Wire009
  Dir = (0,0,-1)
  DirMode = 2
  FaceMakerClass = Part::FaceMakerBullseye
  LengthFwd = -3
  LengthRev = 0
  Solid = true
  Symmetric = false
FEATURE [Part::FeaturePython] Clone041  label="Extrude042"  # Draft clone (typed FeaturePython)
  AttacherType = Attacher::AttachEngine3D
  Fuse = false
  Objects = -> [Extrude031]
  Placement = pos=(-22.75,-4e-15,0) rot=(0,0,1;0rad)
  Scale = (1,1,1)
FEATURE [Part::MultiFuse] Fusion026
  Shapes = -> [Clone041,Extrude030,Clone040,Extrude031]
FEATURE [Part::Cut] Cut030  label="superior008"
  Base = -> Chamfer002
  Tool = -> Fusion026
FEATURE [Part::Feature] path893
  Placement = pos=(-11.0676,7.39298,-9.4) rot=(0,0,1;0rad)
  shape: bbox 22.2 x 39.73 x 2e-07 mm, 0 faces, 0 solids (baked)
FEATURE [Part::Extrusion] Extrude032  label="Extrude043"
  Base = -> path893
  Dir = (0,0,1)
  DirMode = 2
  FaceMakerClass = Part::FaceMakerBullseye
  LengthFwd = 0.2
  LengthRev = 0
  Solid = true
  Symmetric = false
FEATURE [Part::Cut] Cut031  label="inferior001"
  Base = -> Cut027
  Tool = -> Extrude032
FEATURE [Part::Feature] path38055
  Placement = pos=(-7.58747,37.9184,8.5) rot=(0,0,1;0rad)
  shape: bbox 2.735 x 3.175 x 2e-07 mm, 0 faces, 0 solids (baked)
FEATURE [Part::Feature] path38057
  Placement = pos=(-7.58747,37.9184,8.5) rot=(0,0,1;0rad)
  shape: bbox 0.8089 x 3.12 x 2e-07 mm, 0 faces, 0 solids (baked)
FEATURE [Part::Feature] path38057001
  Placement = pos=(-7.58747,37.9184,8.5) rot=(0,0,1;0rad)
  shape: bbox 0.9309 x 0.8474 x 2e-07 mm, 0 faces, 0 solids (baked)
FEATURE [Part::Feature] path38059
  Placement = pos=(-7.58747,37.9184,8.5) rot=(0,0,1;0rad)
  shape: bbox 2.732 x 3.175 x 2e-07 mm, 0 faces, 0 solids (baked)
FEATURE [Part::Feature] path38061
  Placement = pos=(-7.58747,37.9184,8.5) rot=(0,0,1;0rad)
  shape: bbox 2.883 x 4.542 x 2e-07 mm, 0 faces, 0 solids (baked)
FEATURE [Part::Feature] path38061001
  Placement = pos=(-7.58747,37.9184,8.5) rot=(0,0,1;0rad)
  shape: bbox 1.236 x 1.852 x 2e-07 mm, 0 faces, 0 solids (baked)
FEATURE [Part::Feature] path38063
  Placement = pos=(-7.58747,37.9184,8.5) rot=(0,0,1;0rad)
  shape: bbox 0.8089 x 3.12 x 2e-07 mm, 0 faces, 0 solids (baked)
FEATURE [Part::Feature] path38063001
  Placement = pos=(-7.58747,37.9184,8.5) rot=(0,0,1;0rad)
  shape: bbox 0.9309 x 0.8474 x 2e-07 mm, 0 faces, 0 solids (baked)
FEATURE [Part::Feature] path38065
  Placement = pos=(-7.58747,37.9184,8.5) rot=(0,0,1;0rad)
  shape: bbox 2.026 x 3.919 x 2e-07 mm, 0 faces, 0 solids (baked)
FEATURE [Part::Extrusion] Extrude033  label="Extrude044"
  Base = -> path38055
  Dir = (0,0,-1)
  DirMode = 2
  FaceMakerClass = Part::FaceMakerBullseye
  LengthFwd = 0.4
  LengthRev = 0
  Solid = true
  Symmetric = false
FEATURE [Part::Extrusion] Extrude034  label="Extrude045"
  Base = -> path38057
  Dir = (0,0,-1)
  DirMode = 2
  FaceMakerClass = Part::FaceMakerBullseye
  LengthFwd = 0.4
  LengthRev = 0
  Solid = true
  Symmetric = false
FEATURE [Part::Extrusion] Extrude035  label="Extrude046"
  Base = -> path38057001
  Dir = (0,0,-1)
  DirMode = 2
  FaceMakerClass = Part::FaceMakerBullseye
  LengthFwd = 0.4
  LengthRev = 0
  Solid = true
  Symmetric = false
FEATURE [Part::Extrusion] Extrude036  label="Extrude047"
  Base = -> path38059
  Dir = (0,0,-1)
  DirMode = 2
  FaceMakerClass = Part::FaceMakerBullseye
  LengthFwd = 0.4
  LengthRev = 0
  Solid = true
  Symmetric = false
FEATURE [Part::Extrusion] Extrude037  label="Extrude048"
  Base = -> path38061
  Dir = (0,0,-1)
  DirMode = 2
  FaceMakerClass = Part::FaceMakerBullseye
  LengthFwd = 0.4
  LengthRev = 0
  Solid = true
  Symmetric = false
FEATURE [Part::Extrusion] Extrude038  label="Extrude049"
  Base = -> path38063
  Dir = (0,0,-1)
  DirMode = 2
  FaceMakerClass = Part::FaceMakerBullseye
  LengthFwd = 0.4
  LengthRev = 0
  Solid = true
  Symmetric = false
FEATURE [Part::Extrusion] Extrude039  label="Extrude050"
  Base = -> path38063001
  Dir = (0,0,-1)
  DirMode = 2
  FaceMakerClass = Part::FaceMakerBullseye
  LengthFwd = 0.4
  LengthRev = 0
  Solid = true
  Symmetric = false
FEATURE [Part::Extrusion] Extrude040  label="Extrude051"
  Base = -> path38065
  Dir = (0,0,-1)
  DirMode = 2
  FaceMakerClass = Part::FaceMakerBullseye
  LengthFwd = 0.4
  LengthRev = 0
  Solid = true
  Symmetric = false
FEATURE [Part::MultiFuse] Fusion027
  Shapes = -> [Extrude033,Extrude034,Extrude035,Extrude036,Extrude037,Extrude038,Extrude039,Extrude040]
FEATURE [Part::Extrusion] Extrude041  label="Extrude052"
  Base = -> path38061001
  Dir = (0,0,1)
  DirMode = 2
  FaceMakerClass = Part::FaceMakerBullseye
  LengthFwd = -0.4
  LengthRev = 0
  Solid = true
  Symmetric = false
FEATURE [Part::Cut] Cut032
  Base = -> Cut030
  Tool = -> Fusion027
FEATURE [Part::MultiFuse] Fusion028  label="superior009"
  Shapes = -> [Extrude041,Cut032]
